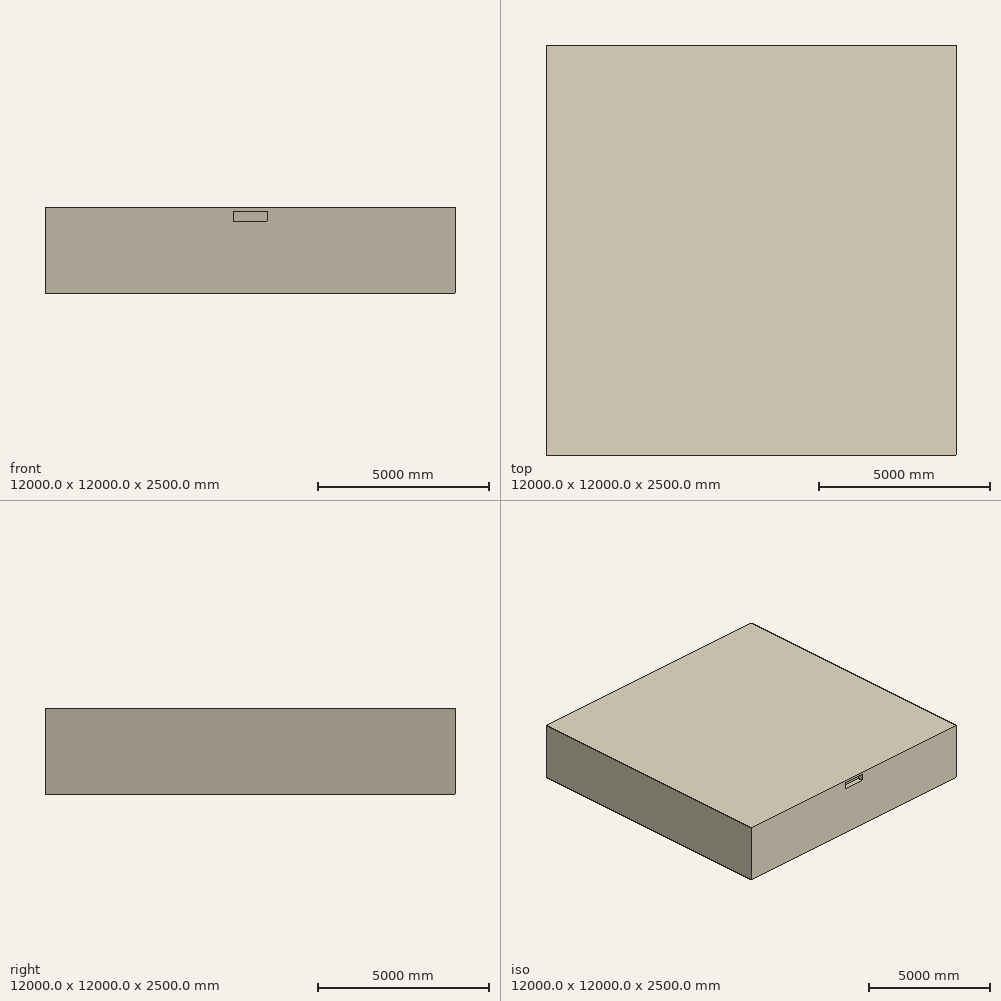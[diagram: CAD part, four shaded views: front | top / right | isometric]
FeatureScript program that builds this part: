
annotation { "Feature Type Name" : "Feature", "Feature Type Description" : "" }
export const myFeature = defineFeature(function(context is Context, id is Id, definition is map)
    precondition{}
    {
        {
            var Q0;
            Q0=qCreatedBy(makeId("Front.planeOp"),FACE);
            var sketch = newSketch(context, id + "F0", { "sketchPlane" : qUnion([Q0])});
            skLineSegment(sketch, "E0.bottom", {"start": v(6000, 1250) * mm, "end": v(-6000, 1250) * mm});
            skLineSegment(sketch, "E0.top", {"start": v(6000, -1250) * mm, "end": v(-6000, -1250) * mm});
            skLineSegment(sketch, "E0.left", {"start": v(6000, 1250) * mm, "end": v(6000, -1250) * mm});
            skLineSegment(sketch, "E0.right", {"start": v(-6000, 1250) * mm, "end": v(-6000, -1250) * mm});
            skPoint(sketch, "E0.middle", {"position": v(0, 0) * mm});
            skSolve(sketch);
        }
        {
            var Q0;
            Q0 = qSketchRegion(id + "F0", true);
            extrude(context, id + "F1", {"entities" : qUnion([Q0]), "oppositeDirection" : true, "depth" : 12000 * mm, "offsetDistance" : 25.4 * mm});
        }
        {
            var Q0;
            Q0=makeQuery(id+"F1.opExtrude","CAP_FACE",FACE,{"disambiguationData":[OSD([sQuery(id+"F0.wireOp",EDGE,"E0.bottom"),sQuery(id+"F0.wireOp",EDGE,"E0.top"),sQuery(id+"F0.wireOp",EDGE,"E0.left"),sQuery(id+"F0.wireOp",EDGE,"E0.right")])],"isStart":true});
            var sketch = newSketch(context, id + "F2", { "sketchPlane" : qUnion([Q0])});
            skLineSegment(sketch, "E1.bottom", {"start": v(-500, 1150) * mm, "end": v(500, 1150) * mm});
            skLineSegment(sketch, "E1.top", {"start": v(-500, 850) * mm, "end": v(500, 850) * mm});
            skLineSegment(sketch, "E1.left", {"start": v(-500, 1150) * mm, "end": v(-500, 850) * mm});
            skLineSegment(sketch, "E1.right", {"start": v(500, 1150) * mm, "end": v(500, 850) * mm});
            skSolve(sketch);
        }
        {
            var Q0;
            Q0=makeQuery(id+"F2.imprint","IMPRINT",FACE,{"disambiguationData":[TD([[makeQuery(id+"F2.imprint","IMPRINT",EDGE,{"derivedFrom":sQuery(id+"F2.wireOp",EDGE,"E1.bottom")}),-1.0]])]});
            extrude(context, id + "F3", {"entities" : qUnion([Q0]), "operationType" : NewBodyOperationType.REMOVE, "oppositeDirection" : true, "depth" : 250 * mm, "offsetDistance" : 25.4 * mm});
        }
    });
